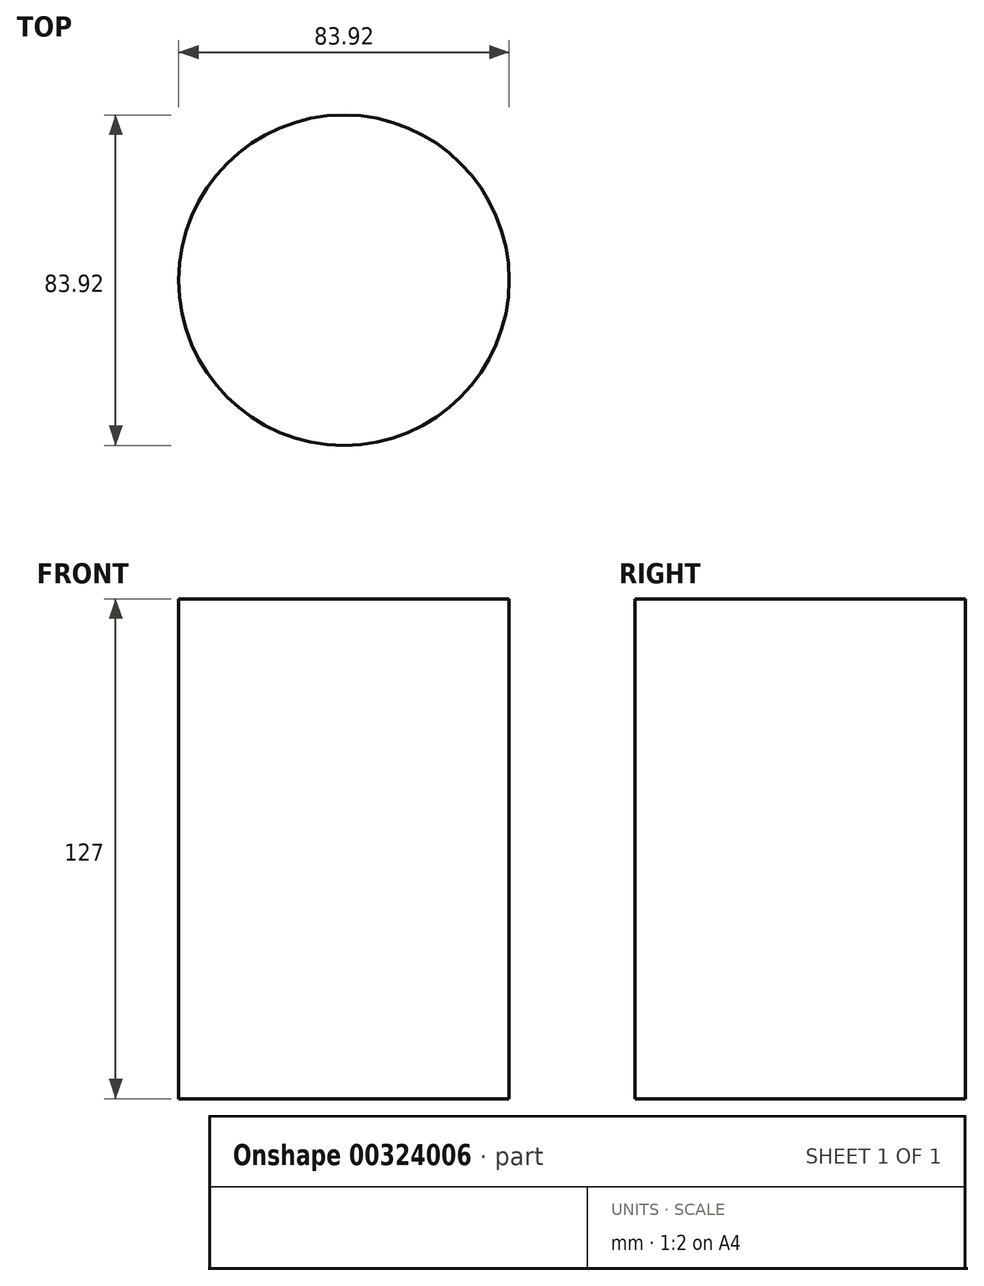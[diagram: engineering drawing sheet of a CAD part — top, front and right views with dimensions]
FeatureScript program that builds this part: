
annotation { "Feature Type Name" : "Feature", "Feature Type Description" : "" }
export const myFeature = defineFeature(function(context is Context, id is Id, definition is map)
    precondition{}
    {
        {
            var Q0;
            Q0=qCreatedBy(makeId("Top.planeOp"),FACE);
            var sketch = newSketch(context, id + "F0", { "sketchPlane" : qUnion([Q0])});
            skCircle(sketch, "E0", {"center": v(0, 0) * mm, "radius": 41.96 * mm});
            skSolve(sketch);
        }
        {
            var Q0;
            Q0=makeQuery(id+"F0.imprint","IMPRINT",FACE,{"disambiguationData":[TD([[makeQuery(id+"F0.imprint","IMPRINT",EDGE,{"derivedFrom":sQuery(id+"F0.wireOp",EDGE,"E0")}),1.0]])]});
            extrude(context, id + "F1", {"entities" : qUnion([Q0]), "depth" : 127 * mm});
        }
    });
